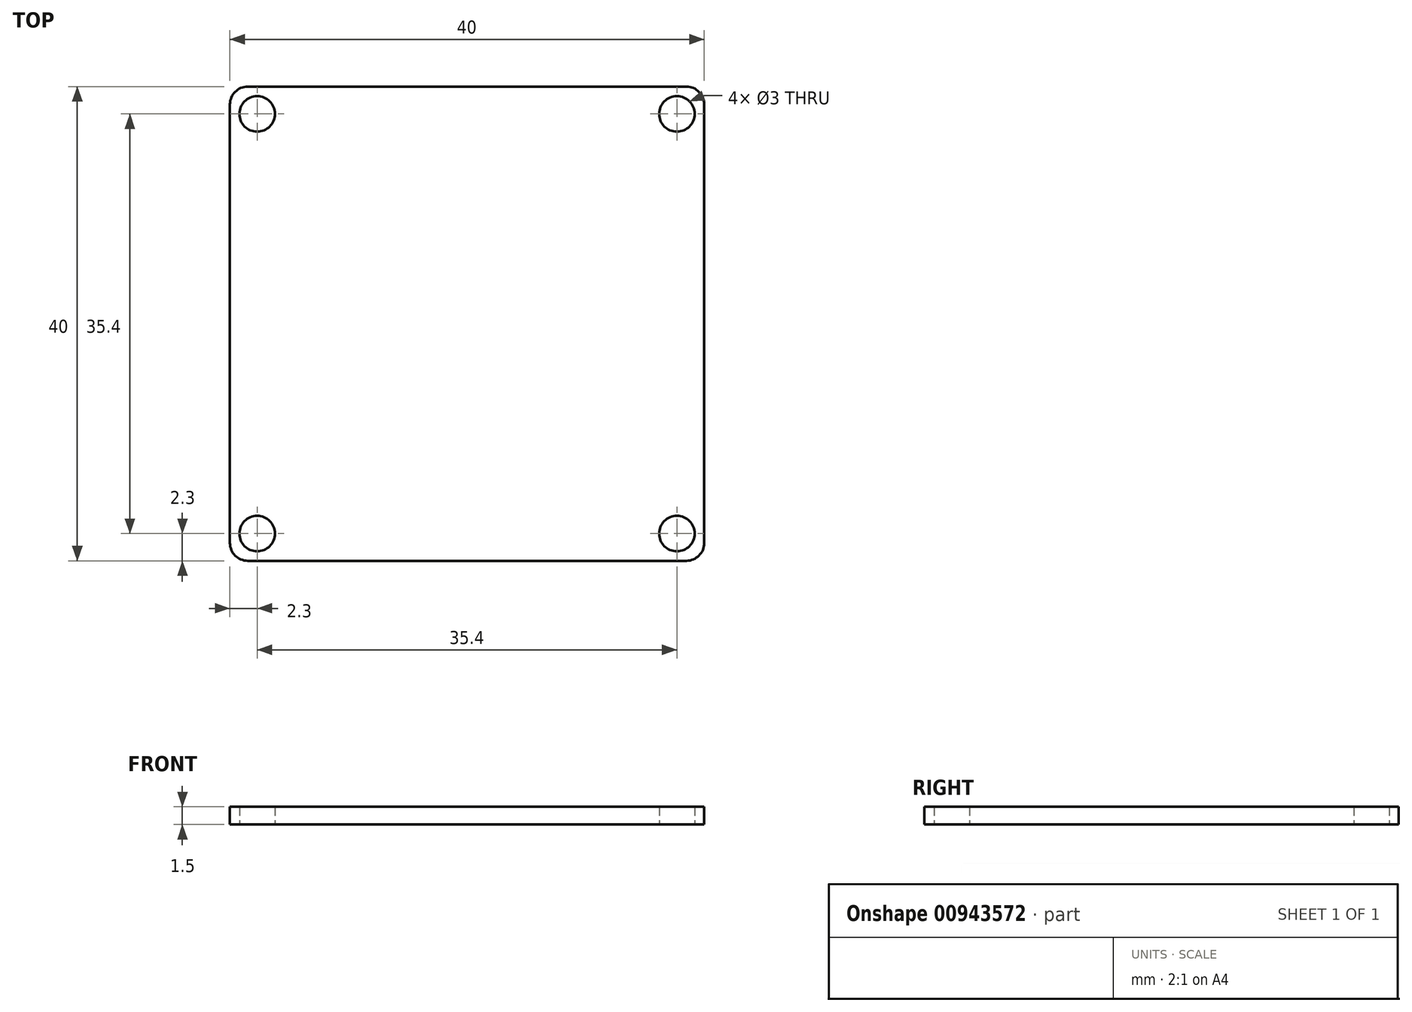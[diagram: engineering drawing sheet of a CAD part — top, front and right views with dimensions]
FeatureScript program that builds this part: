
annotation { "Feature Type Name" : "Feature", "Feature Type Description" : "" }
export const myFeature = defineFeature(function(context is Context, id is Id, definition is map)
    precondition{}
    {
        {
            var Q0;
            Q0=qCreatedBy(makeId("Top.planeOp"),FACE);
            var sketch = newSketch(context, id + "F0", { "sketchPlane" : qUnion([Q0])});
            skLineSegment(sketch, "E0.bottom", {"start": v(-18.5, -20) * mm, "end": v(18.5, -20) * mm});
            skLineSegment(sketch, "E0.top", {"start": v(-18.5, 20) * mm, "end": v(18.5, 20) * mm});
            skLineSegment(sketch, "E0.left", {"start": v(-20, -18.5) * mm, "end": v(-20, 18.5) * mm});
            skLineSegment(sketch, "E0.right", {"start": v(20, -18.5) * mm, "end": v(20, 18.5) * mm});
            skPoint(sketch, "E0.middle", {"position": v(0, 0) * mm});
            skPoint(sketch, "E1.visualSharp", {"position": v(-20, 20) * mm});
            skArc(sketch, "E1.filletArc", {"start": v(-18.5, 20) * mm, "mid": v(-19.56, 19.56) * mm, "end": v(-20, 18.5) * mm});
            skPoint(sketch, "E2.visualSharp", {"position": v(20, 20) * mm});
            skArc(sketch, "E2.filletArc", {"start": v(20, 18.5) * mm, "mid": v(19.56, 19.56) * mm, "end": v(18.5, 20) * mm});
            skPoint(sketch, "E3.visualSharp", {"position": v(-20, -20) * mm});
            skArc(sketch, "E3.filletArc", {"start": v(-20, -18.5) * mm, "mid": v(-19.56, -19.56) * mm, "end": v(-18.5, -20) * mm});
            skPoint(sketch, "E4.visualSharp", {"position": v(20, -20) * mm});
            skArc(sketch, "E4.filletArc", {"start": v(18.5, -20) * mm, "mid": v(19.56, -19.56) * mm, "end": v(20, -18.5) * mm});
            skCircle(sketch, "E5", {"center": v(17.7, 17.7) * mm, "radius": 1.5 * mm});
            skCircle(sketch, "E6.1.0", {"center": v(-17.7, 17.7) * mm, "radius": 1.5 * mm});
            skCircle(sketch, "E6.2.0", {"center": v(-17.7, -17.7) * mm, "radius": 1.5 * mm});
            skCircle(sketch, "E6.3.0", {"center": v(17.7, -17.7) * mm, "radius": 1.5 * mm});
            skSolve(sketch);
        }
        {
            var Q0;
            Q0=makeQuery(id+"F0.imprint","IMPRINT",FACE,{"disambiguationData":[TD([[makeQuery(id+"F0.imprint","IMPRINT",EDGE,{"derivedFrom":sQuery(id+"F0.wireOp",EDGE,"E0.bottom")}),1.0]])]});
            var Q1;
            Q1 = qSketchRegion(id + "F0", true);
            extrude(context, id + "F1", {"entities" : qUnion([Q0, Q1]), "depth" : 1.5 * mm, "offsetDistance" : 25 * mm});
        }
    });
